# Revit family: Storage-Teknion-CTWS_Double_Combination_Wardrobe_Tower-R2021
name_source: partatom
category: Furniture
units: mm (PartAtom-declared; Revit-internal decimal feet)

## family parameters
Always vertical = Yes
Cut with Voids When Loaded = No
OmniClass Number = 23.40.20.00
OmniClass Title = General Furniture and Specialties
Room Calculation Point = No
Shared = Yes
Work Plane-Based = No

## types (6) — shared parameters
Assembly Code = E2020200
Manufacturer = Teknion
Manufacturer Fax = 416.661.4586
Model = CTWS
Product Documentation Link = https://www.teknion.com
Product Line = Chronicle
Product Page URL = https://www.teknion.com
Sustainability Data = https://www.teknion.com
URL = www.teknion.com
Unit Weight URL = http://www.teknion.com
Warranty = http://www.teknion.com
zero-valued in all types: Default Elevation

## per-type parameters (varying)
| type | 2 Box Lower Configuration | Case Finish | Description | File 1 Lower Configuration | File 2 Lower Configuration | Hinged Door Upper Configuration | Hinged Doors Lower Configuration 1 | Open Upper Configuration | Part Number |
| Open Upper, 2 Box 1 File Lower | Yes | Veneer-Teknion-WW-Natural_Veneer_V3-Windsor_Cherry | Double Combination Wardrobe Tower,Open Upper, 2 Box 1 File Lower | No | Yes | No | No | Yes | CTWSOB |
| Open Upper, 2 File Lower | No | Veneer-Teknion-NZ-Natural_Veneer_V3-Natural_Walnut_Flat_Cut | Double Combination Wardrobe Tower,Open Upper, 2 File Lower | Yes | Yes | No | No | Yes | CTWSOF |
| Open Upper, Hinged Doors Lower | No | Veneer - Teknion - VE - Rift White Oak | Double Combination Wardrobe Tower,Open Upper, Hinged Doors Lower | No | No | No | Yes | Yes | CTWSOH |
| Hinged Door Upper, 2 Box 1 File Lower | Yes | Veneer-Teknion-WW-Natural_Veneer_V3-Windsor_Cherry | Double Combination Wardrobe Tower,Hinged Door Upper, 2 Box 1 File Lower | No | Yes | Yes | No | No | CTWSHB |
| Hinged Door Upper, 2 File Lower | No | Veneer-Teknion-NZ-Natural_Veneer_V3-Natural_Walnut_Flat_Cut | Double Combination Wardrobe Tower,Hinged Door Upper, 2 File Lower | Yes | Yes | Yes | No | No | CTWSHF |
| Hinged Door Upper, Hinged Doors Lower | No | Veneer-Teknion-LQ-Natural_Veneer_V3-Poppy_Seed_Flat_Cut | Double Combination Wardrobe Tower,Hinged Door Upper, Hinged Doors Lower | No | No | Yes | Yes | No | CTWSHH |

## geometry (parser evidence)
native form markers: Sweep x2
no freeform markers — native parametric forms only
